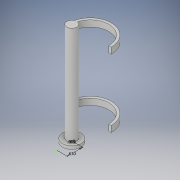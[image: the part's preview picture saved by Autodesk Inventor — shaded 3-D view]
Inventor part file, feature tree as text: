
AUTODESK INVENTOR PART (.ipt)
format: ipt  version: 2017 (Build 210142000, 142)  size: 151,040 bytes
history: native  units: in
note: dims shown in document units (in); Inventor stores cm internally (conversion verified against a paired STEP export)
features: sketch x5, extrude x4, plane x1, projected_geometry x1
ambient origin geometry x8: Origin, YZ Plane, XZ Plane, XY Plane, X Axis, Y Axis, Z Axis, Center Point
bodies: Solid1 (feature_tree)
feature tree (11):
  extrude  "Extrusion1"  Depth=4.0in TaperAngle=0.0deg
  sketch  "Sketch2"  dims[d48=0.1in d49=0.1in]
  plane  "Work Plane2"
  extrude  "Extrusion4"  Depth=0.1in
  extrude  "Extrusion5"  Depth=0.75in
  extrude  "Extrusion6"  Depth=0.25in
  sketch  "Sketch5"  dims[d56=0.25in d57=0.0in d64=0.1in d65=0.1in d66=1.5in d67=0.75in d68=180.0deg d69=0.85in d70=0.25in d71=0.0in d72=0.75in d73=0.125in d74=0.0in d75=0.0625in d76=0.63in d77=0.0312in d78=0.0312in]
  sketch  "Sketch1"  dims[d0=0.4in d1=4.0in d2=0.0in]
  projected_geometry  "Projected Loop1"
  sketch  "Sketch3"  dims[d50=1.5in d51=0.75in]
  sketch  "Sketch4"  dims[d53=180.0deg d55=0.25in]
